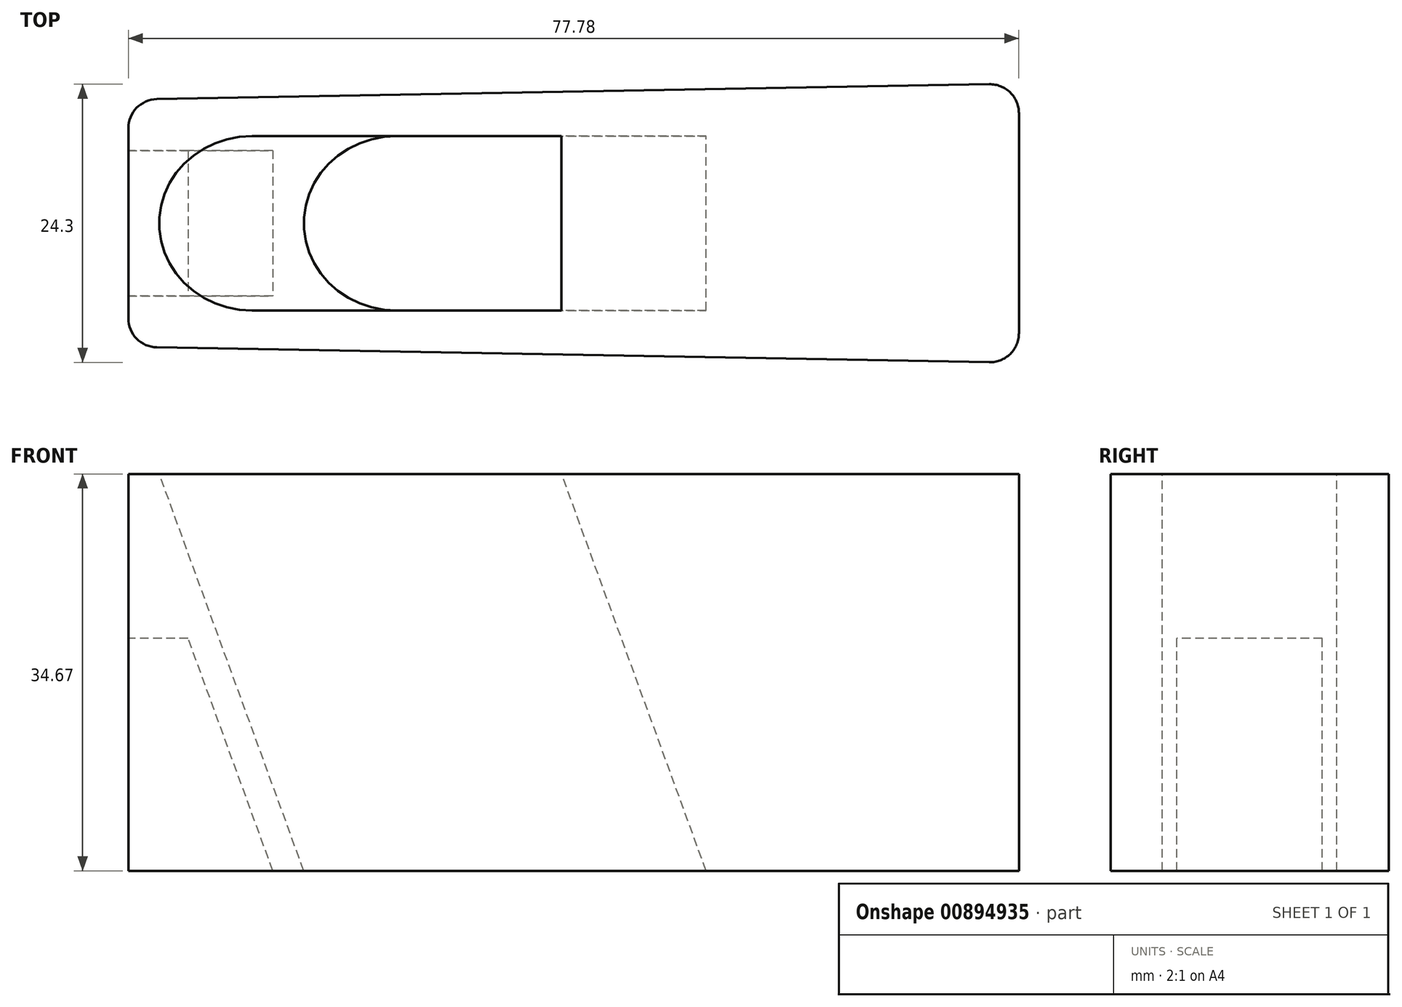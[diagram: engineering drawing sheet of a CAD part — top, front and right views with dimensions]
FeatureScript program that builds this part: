
annotation { "Feature Type Name" : "Feature", "Feature Type Description" : "" }
export const myFeature = defineFeature(function(context is Context, id is Id, definition is map)
    precondition{}
    {
        {
            var Q0;
            Q0=qCreatedBy(makeId("Top.planeOp"),FACE);
            var sketch = newSketch(context, id + "F0", { "sketchPlane" : qUnion([Q0])});
            skLineSegment(sketch, "E0", {"start": v(-38.9, 10.8) * mm, "end": v(-38.9, -10.8) * mm});
            skLineSegment(sketch, "E1", {"start": v(-38.9, -10.8) * mm, "end": v(38.9, -12.2) * mm});
            skLineSegment(sketch, "E2", {"start": v(38.9, -12.2) * mm, "end": v(38.9, 12.2) * mm});
            skLineSegment(sketch, "E3", {"start": v(38.9, 12.2) * mm, "end": v(-38.9, 10.8) * mm});
            skLineSegment(sketch, "E4", {"start": v(-36.97, 0) * mm, "end": v(80.45, 0) * mm, "construction": true});
            skLineSegment(sketch, "E5", {"start": v(0, 25.38) * mm, "end": v(0, -27.59) * mm, "construction": true});
            skSolve(sketch);
        }
        {
            var Q0;
            Q0=makeQuery(id+"F0.imprint","IMPRINT",FACE,{"disambiguationData":[TD([[makeQuery(id+"F0.imprint","IMPRINT",EDGE,{"derivedFrom":sQuery(id+"F0.wireOp",EDGE,"E0")}),1.0]])]});
            extrude(context, id + "F1", {"entities" : qUnion([Q0]), "depth" : 34.67 * mm, "offsetDistance" : 25.4 * mm});
        }
        {
            var Q0;
            Q0=makeQuery(id+"F1.opExtrude","SWEPT_EDGE",EDGE,{"disambiguationData":[OSD([sQuery(id+"F0.wireOp",EDGE,"E0"),sQuery(id+"F0.wireOp",EDGE,"E1")])]});
            var Q1;
            Q1=makeQuery(id+"F1.opExtrude","SWEPT_EDGE",EDGE,{"disambiguationData":[OSD([sQuery(id+"F0.wireOp",EDGE,"E0"),sQuery(id+"F0.wireOp",EDGE,"E3")])]});
            var Q2;
            Q2=makeQuery(id+"F1.opExtrude","SWEPT_EDGE",EDGE,{"disambiguationData":[OSD([sQuery(id+"F0.wireOp",EDGE,"E1"),sQuery(id+"F0.wireOp",EDGE,"E2")])]});
            var Q3;
            Q3=makeQuery(id+"F1.opExtrude","SWEPT_EDGE",EDGE,{"disambiguationData":[OSD([sQuery(id+"F0.wireOp",EDGE,"E2"),sQuery(id+"F0.wireOp",EDGE,"E3")])]});
            fillet(context, id + "F2", {"entities" : qUnion([Q0, Q1, Q2, Q3]), "radius" : 2.54 * mm, "tangentPropagation" : true, "allowEdgeOverflow" : false});
        }
        {
            var Q0;
            Q0=makeQuery(id+"F1.opExtrude","CAP_EDGE",EDGE,{"disambiguationData":[OSD([sQuery(id+"F0.wireOp",EDGE,"E0")])],"isStart":false});
            cPlane(context, id + "F3", {"entities" : qUnion([Q0]), "cplaneType" : CPlaneType.LINE_ANGLE, "offset" : 25.4 * mm, "angle" : 20 * degree, "width" : 152.4 * mm, "height" : 152.4 * mm});
        }
        {
            var Q0;
            Q0=qCreatedBy(id+"F3.planeOp",FACE);
            var sketch = newSketch(context, id + "F4", { "sketchPlane" : qUnion([Q0])});
            skArc(sketch, "E6", {"start": v(-14.53, 7.62) * mm, "mid": v(-22.15, 0) * mm, "end": v(-14.53, -7.62) * mm});
            skLineSegment(sketch, "E7.0", {"start": v(-24.69, -8.3) * mm, "end": v(-24.69, 8.3) * mm, "construction": true});
            skLineSegment(sketch, "E8", {"start": v(-14.53, -7.62) * mm, "end": v(10.87, -7.62) * mm});
            skLineSegment(sketch, "E9", {"start": v(-14.53, 7.62) * mm, "end": v(10.87, 7.62) * mm});
            skLineSegment(sketch, "E10", {"start": v(10.87, 7.62) * mm, "end": v(10.87, -7.62) * mm});
            skSolve(sketch);
        }
        {
            var Q0;
            Q0 = qSketchRegion(id + "F4", true);
            extrude(context, id + "F5", {"entities" : qUnion([Q0]), "operationType" : NewBodyOperationType.REMOVE, "endBound" : BoundingType.THROUGH_ALL, "depth" : 25.4 * mm, "offsetDistance" : 25.4 * mm});
        }
        {
            var Q0;
            Q0=qCreatedBy(makeId("Front.planeOp"),FACE);
            var sketch = newSketch(context, id + "F6", { "sketchPlane" : qUnion([Q0])});
            skPoint(sketch, "E11.0", {"position": v(-36.2, 34.67) * mm});
            skPoint(sketch, "E12.0", {"position": v(-23.57, 0) * mm});
            skLineSegment(sketch, "E13", {"start": v(-36.2, 34.67) * mm, "end": v(-23.57, 0) * mm, "construction": true});
            skCircle(sketch, "E14", {"center": v(-36.2, 34.67) * mm, "radius": 17.78 * mm, "construction": true});
            skLineSegment(sketch, "E15", {"start": v(-26.27, 0) * mm, "end": v(-33.67, 20.32) * mm});
            skLineSegment(sketch, "E16", {"start": v(-33.67, 20.32) * mm, "end": v(-38.9, 20.32) * mm});
            skLineSegment(sketch, "E17.0", {"start": v(-38.9, 0) * mm, "end": v(-38.9, 20.32) * mm});
            skLineSegment(sketch, "E18.0", {"start": v(-36.4, 0) * mm, "end": v(-26.27, 0) * mm});
            skLineSegment(sketch, "E19.0", {"start": v(-36.4, 0) * mm, "end": v(-38.9, 0) * mm});
            skPoint(sketch, "E20.orphan", {"position": v(-38.9, 34.67) * mm});
            skPoint(sketch, "E21.orphan", {"position": v(36.3, 0) * mm});
            skSolve(sketch);
        }
        {
            var Q0;
            Q0 = qSketchRegion(id + "F6", true);
            extrude(context, id + "F7", {"entities" : qUnion([Q0]), "operationType" : NewBodyOperationType.REMOVE, "oppositeDirection" : true, "depth" : 6.35 * mm, "offsetDistance" : 25.4 * mm, "hasSecondDirection" : true, "secondDirectionOppositeDirection" : false, "secondDirectionDepth" : 6.35 * mm});
        }
    });
